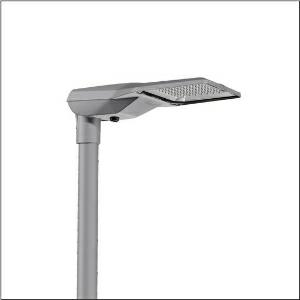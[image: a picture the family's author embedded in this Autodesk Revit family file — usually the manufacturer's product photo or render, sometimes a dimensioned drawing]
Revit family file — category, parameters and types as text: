
# Revit family: streetlight_sl_21_iq_midi___st1_0a_5xe3d31u08mb_cc74
name_source: partatom
category: Lighting Fixtures
units: mm (PartAtom-declared; Revit-internal decimal feet)

## family parameters
Cut with Voids When Loaded = No
Host = Face
Light Source = No
Part Type = Normal
Room Calculation Point = No
Round Connector Dimension = Use Diameter
Shared = No

## types (1)
- --- (1 x LED, 18340 lm, 129.3 W, 3000K)
    Apparent Load = 129 VA
    CIE Flux Codes = 37 72 97 100 100
    Color Rendering = 70
    Color Temperature = 3000K
    Default Elevation = 1800 mm
    Description = Streetlight SL 21 iQ midi, mast luminaire, primary light control with lens, of PMMA, primary optical cover: cover, of toughened safety glass, transparent, light distribution: ST1.0a, light emission: direct distribution, primary light characteristic: asymmetric, installation type: post-top, side-entry, LED, High Power LED, rated luminous flux: 18.340lm, luminous efficacy: 142lm/W, light colour: 730, colour temperature: 3000K, control gear: iQ-Street Remote, D4i with power reduction, control: pre-setting: logarithmic dimming characteristic, Street-Remote, Auto-Match, Temp-Guard, Lumen-Switch, Night-Set, Smart-Wire, Light-Fading, Desk-Remote (wireless, voltage-free reading and setting of iQ features in the workshop via application-optimized NFC function/RFID function), optimised constant luminous flux control (CLO 2.0), mains connection: 230..240V, AC, 50/60Hz, start of lifetime: 129W, end of service life: 142W, reduction: 56W, luminaire housing, of diecast aluminium, powder-coated, SITECO metallic grey (DB 702S), corrosivity category C5 high according to DIN EN ISO 12944, please order mast flange separately, inclination adjustable: 0°, 5°, 10°, 15°, sealing non-destructively replaceable, multi-level sealing system, length: 644mm, width: 335mm, height: 110mm, mast flange for spigot size: 42mm (side-entry): 5XC10008XM4, 60/48mm (side-entry/post-top): 5XC10108XM2, 76/60mm (side-entry/post-top): 5XC10108XM1, mounting height: 4..8m, Smart Interface below, protection rating (complete): IP66, insulation class (complete): insulation class II (safety insulation), certification: CE, ENEC, ENEC+, VDE, impact resistance: IK10, permissible operating ambient temperature for outdoor applications: -40..+50°C, standard-compliant lighting for roads and squares, packaging unit: 1 piece

Light Distribution: ST1.0a
    Height = 111 mm
    Lamp = 1 x LED
    Lamp Light Flux = 18340 lm
    Lamp Power = 129.3 W
    Lamp count = 1
    Length = 644 mm
    Luminous efficacy = 142 lm/W
    Manufacturer = Siteco
    ModVariant = No
    Model = 5XE3D31U08MB
    Number of Poles = 1
    OnlyDefault = Yes
    Power Factor = 1
    Product Name = Streetlight SL 21 iQ midi | ST1.0a
    Product group = mast luminaire | pylon top
    ProductGroupID = 6100
    Protection Class = Protection class II
    Protection Degree = IP 66
    RLX_Detail_Level = 1
    RLX_Emergency_Light_Flux = 0 lm
    RLX_Emergency_Type = 0
    RLX_Emergency_Type_DB = No
    RlxData = <blob elided: 91329 chars, md5=3333fe4a>
    Socket = socket
    Standby Power = 0 W
    System Light Flux = 18340 lm
    System Power = 129 W
    Type Comments = factory setting: luminous flux: 100 % | dim-lin: 254 | 672 mA
    Type Image = l_1004300.jpg
    URL = http://relux.com
    VarID = @adj_114805
    Voltage = 0 V
    Weight = 0.00 kg
    Width = 336 mm

## geometry (parser evidence)
native form markers: Blend x4, Sweep x10
no freeform markers — native parametric forms only
